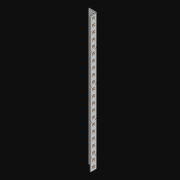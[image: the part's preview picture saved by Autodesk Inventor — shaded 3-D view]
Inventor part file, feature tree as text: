
AUTODESK INVENTOR PART (.ipt)
format: ipt  version: 2021 (Build 250183000, 183)  size: 1,237,504 bytes
history: native  units: in
note: dims shown in document units (in); Inventor stores cm internally (conversion verified against a paired STEP export)
features: extrude x46, other x44, sketch x4, pattern_linear x2, sheet_metal_op x1
ambient origin geometry x8: Origin, YZ Plane, XZ Plane, XY Plane, X Axis, Y Axis, Z Axis, Center Point
bodies: Solid1 (feature_tree)
feature tree (97):
  pattern_linear  "Rectangular Pattern1"  Spacing1=0.5in  [1 undecoded]
  pattern_linear  "Rectangular Pattern3"  Count1=22  [1 undecoded]
  extrude  "Extrusion1"  Depth=0.5in
  extrude  "Extrusion2"  Depth=0.5in
  sketch  "Sketch1"  dims[d0=0.182in]
  other  "Srf1"
  sketch  "Sketch3"  dims[d1=0.063in d2=0.0in]
  other  "Srf3"
  other  "Srf4"
  other  "Srf5"
  other  "Srf6"
  other  "Srf7"
  other  "Srf8"
  other  "Srf9"
  other  "Srf10"
  other  "Srf11"
  other  "Srf12"
  other  "Srf13"
  other  "Srf14"
  other  "Srf15"
  other  "Srf16"
  other  "Srf17"
  other  "Srf18"
  other  "Srf19"
  other  "Srf20"
  other  "Srf21"
  other  "Srf22"
  other  "Srf23"
  other  "Srf24"
  other  "Srf142"
  other  "Srf143"
  other  "Srf144"
  other  "Srf145"
  other  "Srf146"
  other  "Srf147"
  other  "Srf148"
  other  "Srf149"
  other  "Srf150"
  other  "Srf151"
  other  "Srf152"
  other  "Srf153"
  other  "Srf154"
  other  "Srf155"
  other  "Srf156"
  other  "Srf157"
  other  "Srf158"
  other  "Srf159"
  other  "Srf160"
  other  "Srf161"
  other  "Srf162"
  sketch  "Sketch4"  dims[d6=0.182in]
  sketch  "Sketch5"  dims[d7=0.063in d8=0.0in d11=0.5in d12=0.3937in d14=0.5in d18=8.6614in d20=0.5in d21=6.5in d22=0.0in d23=0.841in d24=0.0in]
  sheet_metal_op  "Fold1"
  extrude  "ExtrusionSrf1"  TaperAngle=0.0deg  [1 undecoded]
  extrude  "ExtrusionSrf3"  Depth=0.5in TaperAngle=0.0deg
  extrude  "ExtrusionSrf4"  [1 undecoded]
  extrude  "ExtrusionSrf5"  [1 undecoded]
  extrude  "ExtrusionSrf6"  [1 undecoded]
  extrude  "ExtrusionSrf7"  [1 undecoded]
  extrude  "ExtrusionSrf8"  [1 undecoded]
  extrude  "ExtrusionSrf9"  [1 undecoded]
  extrude  "ExtrusionSrf10"  [1 undecoded]
  extrude  "ExtrusionSrf11"  [1 undecoded]
  extrude  "ExtrusionSrf12"  [1 undecoded]
  extrude  "ExtrusionSrf13"  [1 undecoded]
  extrude  "ExtrusionSrf14"  [1 undecoded]
  extrude  "ExtrusionSrf15"  [1 undecoded]
  extrude  "ExtrusionSrf16"  [1 undecoded]
  extrude  "ExtrusionSrf17"  [1 undecoded]
  extrude  "ExtrusionSrf18"  [1 undecoded]
  extrude  "ExtrusionSrf19"  [1 undecoded]
  extrude  "ExtrusionSrf20"  [1 undecoded]
  extrude  "ExtrusionSrf21"  [1 undecoded]
  extrude  "ExtrusionSrf22"  [1 undecoded]
  extrude  "ExtrusionSrf23"  [1 undecoded]
  extrude  "ExtrusionSrf24"  [1 undecoded]
  extrude  "ExtrusionSrf142"  [1 undecoded]
  extrude  "ExtrusionSrf143"  [1 undecoded]
  extrude  "ExtrusionSrf144"  [1 undecoded]
  extrude  "ExtrusionSrf145"  [1 undecoded]
  extrude  "ExtrusionSrf146"  [1 undecoded]
  extrude  "ExtrusionSrf147"  [1 undecoded]
  extrude  "ExtrusionSrf148"  [1 undecoded]
  extrude  "ExtrusionSrf149"  [1 undecoded]
  extrude  "ExtrusionSrf150"  [1 undecoded]
  extrude  "ExtrusionSrf151"  [1 undecoded]
  extrude  "ExtrusionSrf152"  [1 undecoded]
  extrude  "ExtrusionSrf153"  [1 undecoded]
  extrude  "ExtrusionSrf154"  [1 undecoded]
  extrude  "ExtrusionSrf155"  [1 undecoded]
  extrude  "ExtrusionSrf156"  [1 undecoded]
  extrude  "ExtrusionSrf157"  [1 undecoded]
  extrude  "ExtrusionSrf158"  [1 undecoded]
  extrude  "ExtrusionSrf159"  [1 undecoded]
  extrude  "ExtrusionSrf160"  [1 undecoded]
  extrude  "ExtrusionSrf161"  [1 undecoded]
  extrude  "ExtrusionSrf162"  [1 undecoded]
note: 45 required parameter values undecoded (feature->parameter linkage not recoverable at this tier; creation-order binding heuristic only, values carry confidence <= 0.55)
